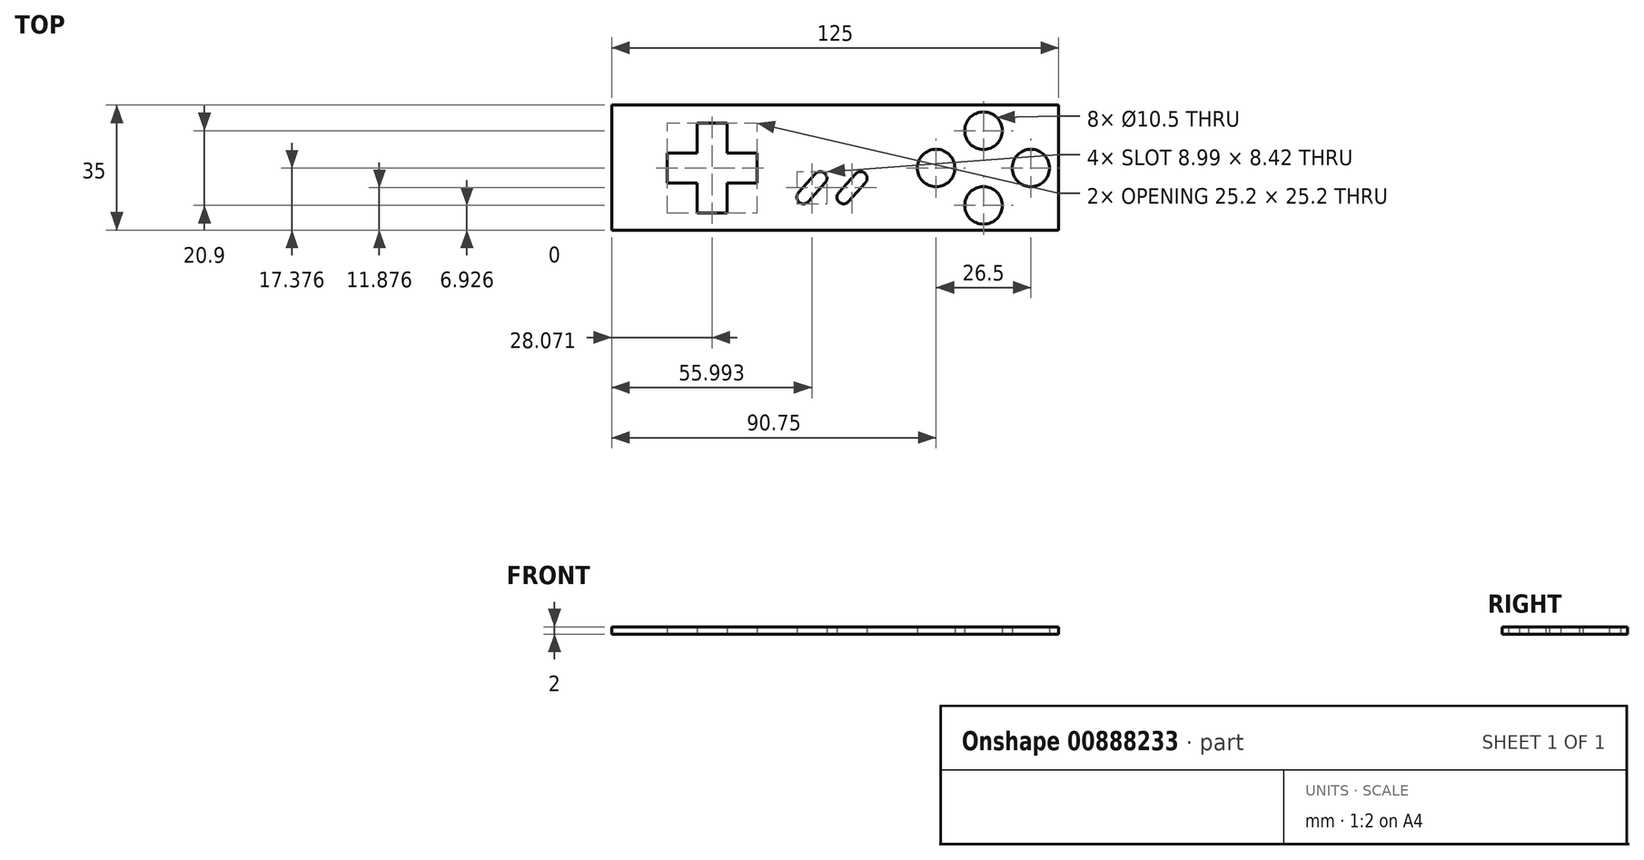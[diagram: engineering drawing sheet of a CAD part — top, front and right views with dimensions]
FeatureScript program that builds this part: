
annotation { "Feature Type Name" : "Feature", "Feature Type Description" : "" }
export const myFeature = defineFeature(function(context is Context, id is Id, definition is map)
    precondition{}
    {
        {
            var Q0;
            Q0=qCreatedBy(makeId("Top.planeOp"),FACE);
            var sketch = newSketch(context, id + "F0", { "sketchPlane" : qUnion([Q0])});
            skLineSegment(sketch, "E0.bottom", {"start": v(-70, 81.46) * mm, "end": v(70, 81.46) * mm});
            skLineSegment(sketch, "E0.top", {"start": v(-70, -81.46) * mm, "end": v(70, -81.46) * mm});
            skLineSegment(sketch, "E0.left", {"start": v(-70, 81.46) * mm, "end": v(-70, -81.46) * mm});
            skLineSegment(sketch, "E0.right", {"start": v(70, 81.46) * mm, "end": v(70, -81.46) * mm});
            skPoint(sketch, "E0.middle", {"position": v(0, 0) * mm});
            skSolve(sketch);
        }
        {
            var Q0;
            Q0=qCreatedBy(makeId("Top.planeOp"),FACE);
            var sketch = newSketch(context, id + "F1", { "sketchPlane" : qUnion([Q0])});
            skCircle(sketch, "E1", {"center": v(41.5, -31.01) * mm, "radius": 5.25 * mm});
            skCircle(sketch, "E2", {"center": v(54.75, -41.46) * mm, "radius": 5.25 * mm});
            skCircle(sketch, "E3", {"center": v(41.5, -51.91) * mm, "radius": 5.25 * mm});
            skCircle(sketch, "E4", {"center": v(28.25, -41.46) * mm, "radius": 5.25 * mm});
            skLineSegment(sketch, "E5", {"start": v(0, 0) * mm, "end": v(0, 93.3) * mm, "construction": true});
            skLineSegment(sketch, "E6", {"start": v(28.25, -41.46) * mm, "end": v(54.75, -41.46) * mm, "construction": true});
            skLineSegment(sketch, "E7", {"start": v(41.5, -31.01) * mm, "end": v(41.5, -51.91) * mm, "construction": true});
            skPoint(sketch, "E8", {"position": v(41.5, -41.46) * mm});
            skLineSegment(sketch, "E9", {"start": v(49.5, -41.46) * mm, "end": v(49.5, -34.98) * mm, "construction": true});
            skLineSegment(sketch, "E10", {"start": v(33.5, -41.46) * mm, "end": v(33.5, -34.95) * mm, "construction": true});
            skLineSegment(sketch, "E11", {"start": v(41.5, -36.26) * mm, "end": v(36.12, -36.26) * mm, "construction": true});
            skLineSegment(sketch, "E12", {"start": v(41.5, -46.66) * mm, "end": v(18.22, -46.66) * mm, "construction": true});
            skLineSegment(sketch, "E13", {"start": v(60, -41.46) * mm, "end": v(60, -34.37) * mm, "construction": true});
            skLineSegment(sketch, "E14", {"start": v(1, -48.38) * mm, "end": v(5.72, -43.08) * mm});
            skLineSegment(sketch, "E15", {"start": v(3.76, -50.84) * mm, "end": v(8.48, -45.54) * mm});
            skArc(sketch, "E16", {"start": v(5.72, -43.08) * mm, "mid": v(8.33, -42.93) * mm, "end": v(8.48, -45.54) * mm});
            skArc(sketch, "E17", {"start": v(3.76, -50.84) * mm, "mid": v(1.14, -51) * mm, "end": v(1, -48.38) * mm});
            skLineSegment(sketch, "E18", {"start": v(7.1, -42.46) * mm, "end": v(12.22, -42.46) * mm, "construction": true});
            skLineSegment(sketch, "E19", {"start": v(2.38, -51.46) * mm, "end": v(12.22, -51.46) * mm, "construction": true});
            skLineSegment(sketch, "E20", {"start": v(12.22, -51.46) * mm, "end": v(12.22, -42.46) * mm, "construction": true});
            skLineSegment(sketch, "E21", {"start": v(1.14, -51) * mm, "end": v(8.33, -42.93) * mm, "construction": true});
            skLineSegment(sketch, "E22", {"start": v(0.53, -49.61) * mm, "end": v(0.53, -44.5) * mm, "construction": true});
            skLineSegment(sketch, "E23", {"start": v(8.95, -44.31) * mm, "end": v(8.95, -30.23) * mm, "construction": true});
            skPoint(sketch, "E24", {"position": v(4.74, -46.96) * mm});
            skLineSegment(sketch, "E25.1.0.0", {"start": v(-10.25, -48.38) * mm, "end": v(-5.53, -43.08) * mm});
            skArc(sketch, "E25.1.0.1", {"start": v(-5.53, -43.08) * mm, "mid": v(-2.91, -42.93) * mm, "end": v(-2.76, -45.54) * mm});
            skLineSegment(sketch, "E25.1.0.2", {"start": v(-7.49, -50.84) * mm, "end": v(-2.76, -45.54) * mm});
            skArc(sketch, "E25.1.0.3", {"start": v(-7.49, -50.84) * mm, "mid": v(-10.1, -51) * mm, "end": v(-10.25, -48.38) * mm});
            skLineSegment(sketch, "E25.direction1", {"start": v(1, -48.38) * mm, "end": v(-10.25, -48.38) * mm, "construction": true});
            skPoint(sketch, "E26", {"position": v(-5.3, -48.38) * mm});
            skLineSegment(sketch, "E27", {"start": v(-10.72, -55.05) * mm, "end": v(-10.72, -49.61) * mm, "construction": true});
            skLineSegment(sketch, "E28", {"start": v(-30.23, -37.26) * mm, "end": v(-21.83, -37.26) * mm});
            skLineSegment(sketch, "E29", {"start": v(-21.83, -37.26) * mm, "end": v(-21.83, -45.66) * mm});
            skLineSegment(sketch, "E30", {"start": v(-21.83, -45.66) * mm, "end": v(-30.23, -45.66) * mm});
            skLineSegment(sketch, "E31", {"start": v(-30.23, -37.26) * mm, "end": v(-30.23, -28.86) * mm});
            skLineSegment(sketch, "E32", {"start": v(-30.23, -28.86) * mm, "end": v(-38.63, -28.86) * mm});
            skLineSegment(sketch, "E33", {"start": v(-38.63, -28.86) * mm, "end": v(-38.63, -37.26) * mm});
            skLineSegment(sketch, "E34", {"start": v(-38.63, -37.26) * mm, "end": v(-47.03, -37.26) * mm});
            skLineSegment(sketch, "E35", {"start": v(-47.03, -37.26) * mm, "end": v(-47.03, -45.66) * mm});
            skLineSegment(sketch, "E36", {"start": v(-47.03, -45.66) * mm, "end": v(-38.63, -45.66) * mm});
            skLineSegment(sketch, "E37", {"start": v(-38.63, -45.66) * mm, "end": v(-38.63, -54.06) * mm});
            skLineSegment(sketch, "E38", {"start": v(-38.63, -54.06) * mm, "end": v(-30.23, -54.06) * mm});
            skLineSegment(sketch, "E39", {"start": v(-30.23, -54.06) * mm, "end": v(-30.23, -45.66) * mm});
            skPoint(sketch, "E40", {"position": v(-21.83, -41.46) * mm});
            skLineSegment(sketch, "E41", {"start": v(-21.83, -41.46) * mm, "end": v(28.25, -41.46) * mm, "construction": true});
            skLineSegment(sketch, "E42", {"start": v(6.12, -48.2) * mm, "end": v(3.36, -45.73) * mm});
            skSolve(sketch);
        }
        {
            var Q0;
            Q0=qCreatedBy(makeId("Top.planeOp"),FACE);
            var sketch = newSketch(context, id + "F2", { "sketchPlane" : qUnion([Q0])});
            skLineSegment(sketch, "E43.bottom", {"start": v(62.5, -23.84) * mm, "end": v(-62.5, -23.84) * mm});
            skLineSegment(sketch, "E43.top", {"start": v(62.5, -58.84) * mm, "end": v(-62.5, -58.84) * mm});
            skLineSegment(sketch, "E43.left", {"start": v(62.5, -23.84) * mm, "end": v(62.5, -58.84) * mm});
            skLineSegment(sketch, "E43.right", {"start": v(-62.5, -23.84) * mm, "end": v(-62.5, -58.84) * mm});
            skPoint(sketch, "E43.middle", {"position": v(0, -41.34) * mm});
            skSolve(sketch);
        }
        {
            var Q0;
            Q0 = qSketchRegion(id + "F2", true);
            extrude(context, id + "F3", {"entities" : qUnion([Q0]), "depth" : 2 * mm, "offsetDistance" : 25 * mm});
        }
        {
            var Q0;
            Q0 = qSketchRegion(id + "F1", true);
            extrude(context, id + "F4", {"entities" : qUnion([Q0]), "operationType" : NewBodyOperationType.REMOVE, "depth" : 25 * mm, "offsetDistance" : 25 * mm});
        }
    });
